# Revit family: Sanitary_Shower-screens_Duscholux_Giro_Fixed-Segment+Pivot-door-shower
name_source: partatom
category: Plumbing Fixtures
revit_build: Autodesk Revit 2016 (Build: 20150220_1215(x64)
units: mm (PartAtom-declared; Revit-internal decimal feet)

## family parameters
Always vertical = Yes
Cut with Voids When Loaded = No
OmniClass Number = 23.45.00.00
OmniClass Title = Sanitary, Laundry, and Cleaning Equipment
Part Type = Normal
Room Calculation Point = No
Round Connector Dimension = Use Diameter
Shared = No
Work Plane-Based = No

## types (3) — shared parameters
Assembly Code = C1030200
Brand = Duscholux
Certified Quality UNE EN 14428 = http://www.duscholux.es
Combinations = Lateral 90° / Lateral180°
Components = Eropean components
Configuration enclosure = http://configuratumampara.duscholux.es
Description = Front 1 Fixed segment + 1 pivot door at 180° for shower
Edition number = 1
Environmental Management ISO 14001 = ECOEMBES Certificate
Fact Sheet = http://blob.duscholux.es
Glass Material = Glass_Material-Duscholux
Glass height = 1892 mm  [stored 6.20735 ft]
Glass in Building UNE EN 12150 = CE Conformity marking
Handle Height = 950 mm  [stored 3.1168 ft]
Height = 1900 mm  [stored 6.2336 ft]
IFC Classification = Furnishing Element
Image = http://www.duscholux.es
Maintenance and Cleaning = http://www.duscholux.es
Manufacturer = Duscholux Ibérica, S.A.
Manufacturer country = Spain
Manufacturer name = Duscholux Ibérica, S.A.
Max Height = 1900 mm  [stored 6.2336 ft]
NBS Reference Code = 45-35-70
NBS Reference Description = Shower Enclosures
Net Weight (Kg) = 30
Opening System = Pivot Door
Opening System Image = http://blob.duscholux.es
Opening angle = 0.00°
Product family = Plus Evolution Giro
Product group = Front for shower
Products = http://www.duscholux.es
Ref. = 7BA / 7BC
Series = Plus Evolution Giro
Technical Inspection Certificate (Applus) = http://www.duscholux.es
Thickness Glass = 5 mm  [stored 0.0164042 ft]
UNSPSC Code = 30181507
URL = http://www.duscholux.es
Uniclass 2015 Code = PR-40-20-06-79
Uniclass 2015 Description = Shower Enclosures

## per-type parameters (varying)
| type | Accesories Material | Design country | Door Aperture | Frame Material | Handle Material | Min Max Width | Width |
| Shiny silver Finish | Plastic, Gray | Spain / Germany | 639 mm | Shiny Silver  Aluminium Finish | Matt Silver Aluminium Finish | 900 mm  [stored 2.95276 ft] | 900 mm  [stored 2.95276 ft] |
| White Aluminium Finish | White Finish | Eropean components | 539 mm  [stored 1.76837 ft] | White Aluminium Finish | White Finish | 800 mm  [stored 2.62467 ft] | 800 mm  [stored 2.62467 ft] |
| Silver Matt Aluminium Finish | Plastic, Gray | Spain / Germany | 639 mm | Matt Silver Aluminium Finish | Matt Silver Aluminium Finish | 900 mm  [stored 2.95276 ft] | 900 mm  [stored 2.95276 ft] |

note: [stored X ft] marks values corroborated as IEEE doubles in the binary element streams (Revit-internal decimal feet)

## geometry (parser evidence)
native form markers: Sweep x3
no freeform markers — native parametric forms only
